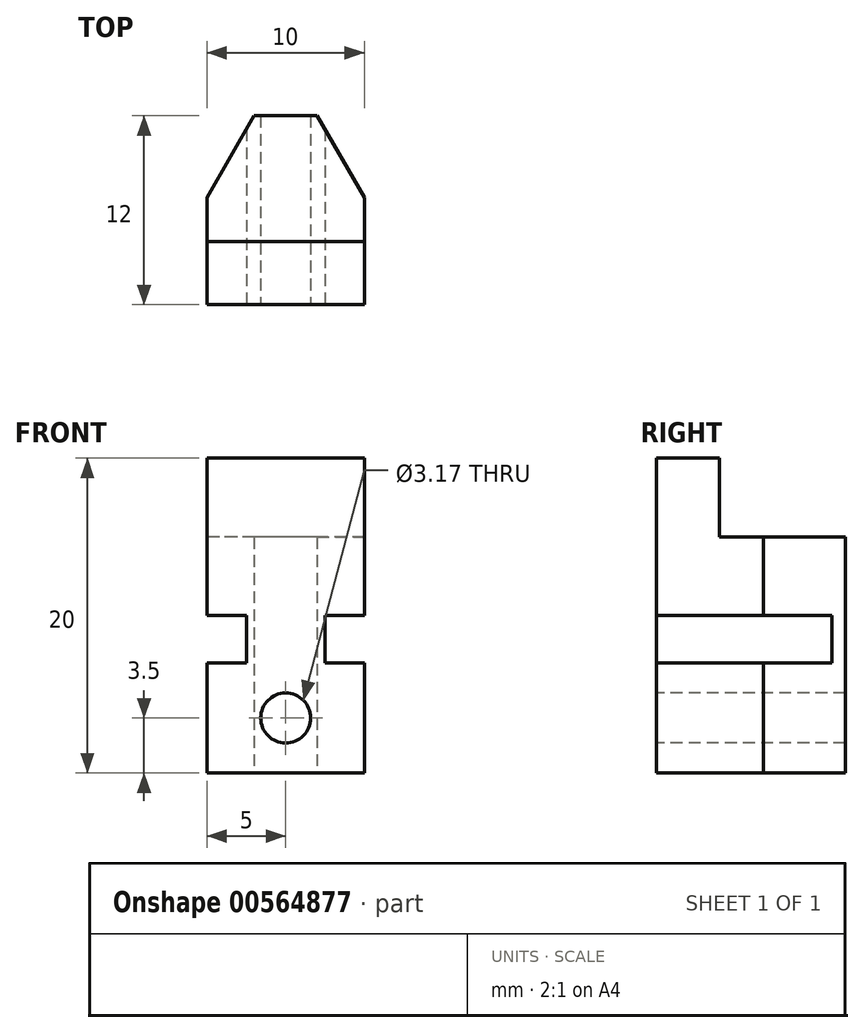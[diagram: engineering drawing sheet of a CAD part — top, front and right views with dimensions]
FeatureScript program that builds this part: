
annotation { "Feature Type Name" : "Feature", "Feature Type Description" : "" }
export const myFeature = defineFeature(function(context is Context, id is Id, definition is map)
    precondition{}
    {
        {
            var Q0;
            Q0=qCreatedBy(makeId("Top.planeOp"),FACE);
            var sketch = newSketch(context, id + "F0", { "sketchPlane" : qUnion([Q0])});
            skLineSegment(sketch, "E0", {"start": v(0, 0) * mm, "end": v(5, 0) * mm});
            skLineSegment(sketch, "E1", {"start": v(5, 0) * mm, "end": v(5, 6.8) * mm});
            skLineSegment(sketch, "E2", {"start": v(5, 6.8) * mm, "end": v(2, 12) * mm});
            skLineSegment(sketch, "E3", {"start": v(2, 12) * mm, "end": v(0, 12) * mm});
            skLineSegment(sketch, "E4", {"start": v(0, 12) * mm, "end": v(0, 0) * mm});
            skSolve(sketch);
        }
        {
            var Q0;
            Q0=makeQuery(id+"F0.imprint","IMPRINT",FACE,{"disambiguationData":[TD([[makeQuery(id+"F0.imprint","IMPRINT",EDGE,{"derivedFrom":sQuery(id+"F0.wireOp",EDGE,"E0")}),1.0]])]});
            extrude(context, id + "F1", {"entities" : qUnion([Q0]), "depth" : 20 * mm, "offsetDistance" : 25.4 * mm});
        }
        {
            var Q0;
            Q0=makeQuery(id+"F1.opExtrude","SWEPT_FACE",FACE,{"disambiguationData":[OSD([sQuery(id+"F0.wireOp",EDGE,"E4")])]});
            var sketch = newSketch(context, id + "F2", { "sketchPlane" : qUnion([Q0])});
            skLineSegment(sketch, "E5.bottom", {"start": v(-12, 20) * mm, "end": v(-4, 20) * mm});
            skLineSegment(sketch, "E5.top", {"start": v(-12, 15) * mm, "end": v(-4, 15) * mm});
            skLineSegment(sketch, "E5.left", {"start": v(-12, 20) * mm, "end": v(-12, 15) * mm});
            skLineSegment(sketch, "E5.right", {"start": v(-4, 20) * mm, "end": v(-4, 15) * mm});
            skSolve(sketch);
        }
        {
            var Q0;
            Q0=makeQuery(id+"F2.imprint","IMPRINT",FACE,{"disambiguationData":[TD([[makeQuery(id+"F2.imprint","IMPRINT",EDGE,{"derivedFrom":sQuery(id+"F2.wireOp",EDGE,"E5.bottom")}),-1.0]])]});
            extrude(context, id + "F3", {"entities" : qUnion([Q0]), "operationType" : NewBodyOperationType.REMOVE, "oppositeDirection" : true, "depth" : 25.4 * mm, "offsetDistance" : 25.4 * mm});
        }
        {
            var Q0;
            Q0=makeQuery(id+"F1.opExtrude","SWEPT_FACE",FACE,{"disambiguationData":[OSD([sQuery(id+"F0.wireOp",EDGE,"E0")])]});
            var sketch = newSketch(context, id + "F4", { "sketchPlane" : qUnion([Q0])});
            skLineSegment(sketch, "E6.bottom", {"start": v(5, 7) * mm, "end": v(2.5, 7) * mm});
            skLineSegment(sketch, "E6.top", {"start": v(5, 10) * mm, "end": v(2.5, 10) * mm});
            skLineSegment(sketch, "E6.left", {"start": v(5, 7) * mm, "end": v(5, 10) * mm});
            skLineSegment(sketch, "E6.right", {"start": v(2.5, 7) * mm, "end": v(2.5, 10) * mm});
            skSolve(sketch);
        }
        {
            var Q0;
            Q0=makeQuery(id+"F4.imprint","IMPRINT",FACE,{"disambiguationData":[TD([[makeQuery(id+"F4.imprint","IMPRINT",EDGE,{"derivedFrom":sQuery(id+"F4.wireOp",EDGE,"E6.bottom")}),-1.0]])]});
            extrude(context, id + "F5", {"entities" : qUnion([Q0]), "operationType" : NewBodyOperationType.REMOVE, "oppositeDirection" : true, "depth" : 38.1 * mm, "offsetDistance" : 25.4 * mm});
        }
        {
            var Q0;
            Q0=makeQuery(id+"F1.opExtrude","SWEPT_BODY",BODY,{"disambiguationData":[OSD([sQuery(id+"F0.wireOp",EDGE,"E0"),sQuery(id+"F0.wireOp",EDGE,"E1"),sQuery(id+"F0.wireOp",EDGE,"E2"),sQuery(id+"F0.wireOp",EDGE,"E3"),sQuery(id+"F0.wireOp",EDGE,"E4")])]});
            var Q1;
            Q1=makeQuery(id+"F1.opExtrude","SWEPT_FACE",FACE,{"disambiguationData":[OSD([sQuery(id+"F0.wireOp",EDGE,"E4")])]});
            mirror(context, id + "F6", {"operationType" : NewBodyOperationType.ADD, "entities" : qUnion([Q0]), "mirrorPlane" : qUnion([Q1])});
        }
        {
            var Q0;
            {var subQ0=makeQuery(id+"F1.opExtrude","SWEPT_FACE",FACE,{"disambiguationData":[OSD([sQuery(id+"F0.wireOp",EDGE,"E0")])]});Q0=makeQuery(id+"F6.boolean.opBoolean","MERGE",FACE,{"derivedFrom":[subQ0,makeQuery(id+"F6.opPattern","COPY",FACE,{"derivedFrom":subQ0,"instanceName":"1"})]});}
            var sketch = newSketch(context, id + "F7", { "sketchPlane" : qUnion([Q0])});
            skCircle(sketch, "E7", {"center": v(0, 3.5) * mm, "radius": 1.59 * mm});
            skSolve(sketch);
        }
        {
            var Q0;
            Q0=makeQuery(id+"F7.imprint","IMPRINT",FACE,{"disambiguationData":[TD([[makeQuery(id+"F7.imprint","IMPRINT",EDGE,{"derivedFrom":sQuery(id+"F7.wireOp",EDGE,"E7")}),1.0]])]});
            extrude(context, id + "F8", {"entities" : qUnion([Q0]), "operationType" : NewBodyOperationType.REMOVE, "oppositeDirection" : true, "depth" : 25.4 * mm, "offsetDistance" : 25.4 * mm});
        }
    });
